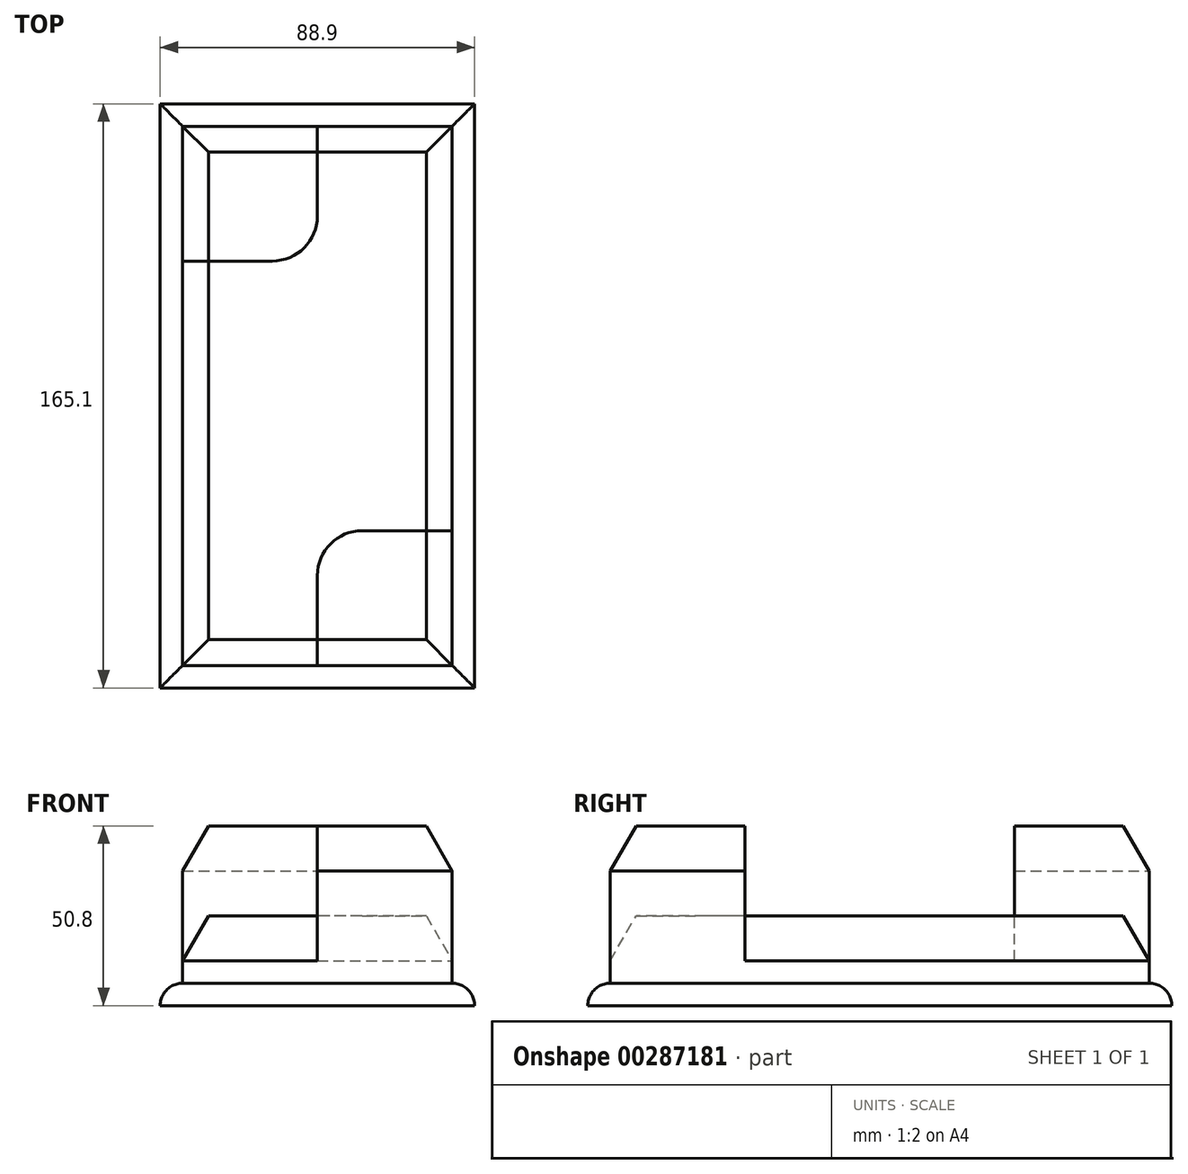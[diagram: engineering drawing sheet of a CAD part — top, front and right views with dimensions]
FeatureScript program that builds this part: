
annotation { "Feature Type Name" : "Feature", "Feature Type Description" : "" }
export const myFeature = defineFeature(function(context is Context, id is Id, definition is map)
    precondition{}
    {
        {
            var Q0;
            Q0=qCreatedBy(makeId("Top.planeOp"),FACE);
            var sketch = newSketch(context, id + "F0", { "sketchPlane" : qUnion([Q0])});
            skLineSegment(sketch, "E0.bottom", {"start": v(38.1, 76.2) * mm, "end": v(-38.1, 76.2) * mm});
            skLineSegment(sketch, "E0.top", {"start": v(38.1, -76.2) * mm, "end": v(-38.1, -76.2) * mm});
            skLineSegment(sketch, "E0.left", {"start": v(38.1, 76.2) * mm, "end": v(38.1, -76.2) * mm});
            skLineSegment(sketch, "E0.right", {"start": v(-38.1, 76.2) * mm, "end": v(-38.1, -76.2) * mm});
            skPoint(sketch, "E0.middle", {"position": v(0, 0) * mm});
            skLineSegment(sketch, "E1", {"start": v(-38.1, 38.1) * mm, "end": v(-12.7, 38.1) * mm});
            skLineSegment(sketch, "E2", {"start": v(0, 50.8) * mm, "end": v(0, 76.2) * mm});
            skLineSegment(sketch, "E3", {"start": v(0, -76.2) * mm, "end": v(0, -50.8) * mm});
            skLineSegment(sketch, "E4", {"start": v(12.7, -38.1) * mm, "end": v(38.1, -38.1) * mm});
            skPoint(sketch, "E5.visualSharp", {"position": v(0, 38.1) * mm});
            skArc(sketch, "E5.filletArc", {"start": v(-12.7, 38.1) * mm, "mid": v(-3.72, 41.82) * mm, "end": v(0, 50.8) * mm});
            skPoint(sketch, "E6.visualSharp", {"position": v(0, -38.1) * mm});
            skArc(sketch, "E6.filletArc", {"start": v(12.7, -38.1) * mm, "mid": v(3.72, -41.82) * mm, "end": v(0, -50.8) * mm});
            skLineSegment(sketch, "E7.0", {"start": v(44.45, 82.55) * mm, "end": v(-44.45, 82.55) * mm});
            skLineSegment(sketch, "E7.1", {"start": v(44.45, 82.55) * mm, "end": v(44.45, -82.55) * mm});
            skLineSegment(sketch, "E7.2", {"start": v(44.45, -82.55) * mm, "end": v(-44.45, -82.55) * mm});
            skLineSegment(sketch, "E7.3", {"start": v(-44.45, 82.55) * mm, "end": v(-44.45, -82.55) * mm});
            skSolve(sketch);
        }
        {
            var Q0;
            Q0=makeQuery(id+"F0.imprint","IMPRINT",FACE,{"disambiguationData":[TD([[makeQuery(id+"F0.imprint","IMPRINT",EDGE,{"derivedFrom":sQuery(id+"F0.wireOp",EDGE,"E7.0")}),1.0]])]});
            extrude(context, id + "F1", {"entities" : qUnion([Q0]), "depth" : 6.35 * mm});
        }
        {
            var Q0;
            {var subQ3=sQuery(id+"F0.wireOp",EDGE,"E1");Q0=makeQuery(id+"F0.imprint","IMPRINT",FACE,{"disambiguationData":[TD([[makeQuery(id+"F0.imprint","IMPRINT",EDGE,{"derivedFrom":subQ3}),-1.0]])]});}
            extrude(context, id + "F2", {"entities" : qUnion([Q0]), "operationType" : NewBodyOperationType.ADD, "depth" : 25.4 * mm});
        }
        {
            var Q0;
            {var subQ1=sQuery(id+"F0.wireOp",EDGE,"E3");Q0=makeQuery(id+"F0.imprint","IMPRINT",FACE,{"disambiguationData":[TD([[makeQuery(id+"F0.imprint","IMPRINT",EDGE,{"derivedFrom":subQ1}),-1.0]])]});}
            var Q1;
            {var subQ1=sQuery(id+"F0.wireOp",EDGE,"E1");Q1=makeQuery(id+"F0.imprint","IMPRINT",FACE,{"disambiguationData":[TD([[makeQuery(id+"F0.imprint","IMPRINT",EDGE,{"derivedFrom":subQ1}),1.0]])]});}
            extrude(context, id + "F3", {"entities" : qUnion([Q0, Q1]), "operationType" : NewBodyOperationType.ADD, "depth" : 50.8 * mm});
        }
        {
            var Q0;
            Q0=makeQuery(id+"F1.opExtrude","CAP_EDGE",EDGE,{"disambiguationData":[OSD([sQuery(id+"F0.wireOp",EDGE,"E7.2")])],"isStart":false});
            var Q1;
            Q1=makeQuery(id+"F1.opExtrude","CAP_EDGE",EDGE,{"disambiguationData":[OSD([sQuery(id+"F0.wireOp",EDGE,"E7.1")])],"isStart":false});
            var Q2;
            Q2=makeQuery(id+"F1.opExtrude","CAP_EDGE",EDGE,{"disambiguationData":[OSD([sQuery(id+"F0.wireOp",EDGE,"E7.3")])],"isStart":false});
            var Q3;
            Q3=makeQuery(id+"F1.opExtrude","CAP_EDGE",EDGE,{"disambiguationData":[OSD([sQuery(id+"F0.wireOp",EDGE,"E7.0")])],"isStart":false});
            fillet(context, id + "F4", {"entities" : qUnion([Q0, Q1, Q2, Q3]), "radius" : 6.35 * mm, "tangentPropagation" : true, "allowEdgeOverflow" : false});
        }
        {
            var Q0;
            Q0=makeQuery(id+"F2.opExtrude","CAP_EDGE",EDGE,{"disambiguationData":[OSD([sQuery(id+"F0.wireOp",EDGE,"E0.left")])],"isStart":false});
            var Q1;
            Q1=makeQuery(id+"F2.opExtrude","CAP_EDGE",EDGE,{"disambiguationData":[OSD([sQuery(id+"F0.wireOp",EDGE,"E0.bottom")])],"isStart":false});
            var Q2;
            Q2=makeQuery(id+"F2.opExtrude","CAP_EDGE",EDGE,{"disambiguationData":[OSD([sQuery(id+"F0.wireOp",EDGE,"E0.right")])],"isStart":false});
            var Q3;
            Q3=makeQuery(id+"F2.opExtrude","CAP_EDGE",EDGE,{"disambiguationData":[OSD([sQuery(id+"F0.wireOp",EDGE,"E0.top")])],"isStart":false});
            chamfer(context, id + "F5", {"entities" : qUnion([Q0, Q1, Q2, Q3]), "chamferType" : ChamferType.OFFSET_ANGLE, "width" : 12.7 * mm, "oppositeDirection" : false, "angle" : 30 * degree, "tangentPropagation" : true});
        }
        {
            var Q0;
            Q0=makeQuery(id+"F3.opExtrude","CAP_EDGE",EDGE,{"disambiguationData":[OSD([sQuery(id+"F0.wireOp",EDGE,"E0.left")])],"isStart":false});
            var Q1;
            Q1=makeQuery(id+"F3.opExtrude","CAP_EDGE",EDGE,{"disambiguationData":[OSD([sQuery(id+"F0.wireOp",EDGE,"E0.top")])],"isStart":false});
            chamfer(context, id + "F6", {"entities" : qUnion([Q0, Q1]), "chamferType" : ChamferType.OFFSET_ANGLE, "width" : 12.7 * mm, "oppositeDirection" : false, "angle" : 30 * degree, "tangentPropagation" : true});
        }
        {
            var Q0;
            Q0=makeQuery(id+"F3.opExtrude","CAP_EDGE",EDGE,{"disambiguationData":[OSD([sQuery(id+"F0.wireOp",EDGE,"E0.bottom")])],"isStart":false});
            var Q1;
            Q1=makeQuery(id+"F3.opExtrude","CAP_EDGE",EDGE,{"disambiguationData":[OSD([sQuery(id+"F0.wireOp",EDGE,"E0.right")])],"isStart":false});
            chamfer(context, id + "F7", {"entities" : qUnion([Q0, Q1]), "chamferType" : ChamferType.OFFSET_ANGLE, "width" : 12.7 * mm, "oppositeDirection" : true, "angle" : 30 * degree, "tangentPropagation" : true});
        }
    });
